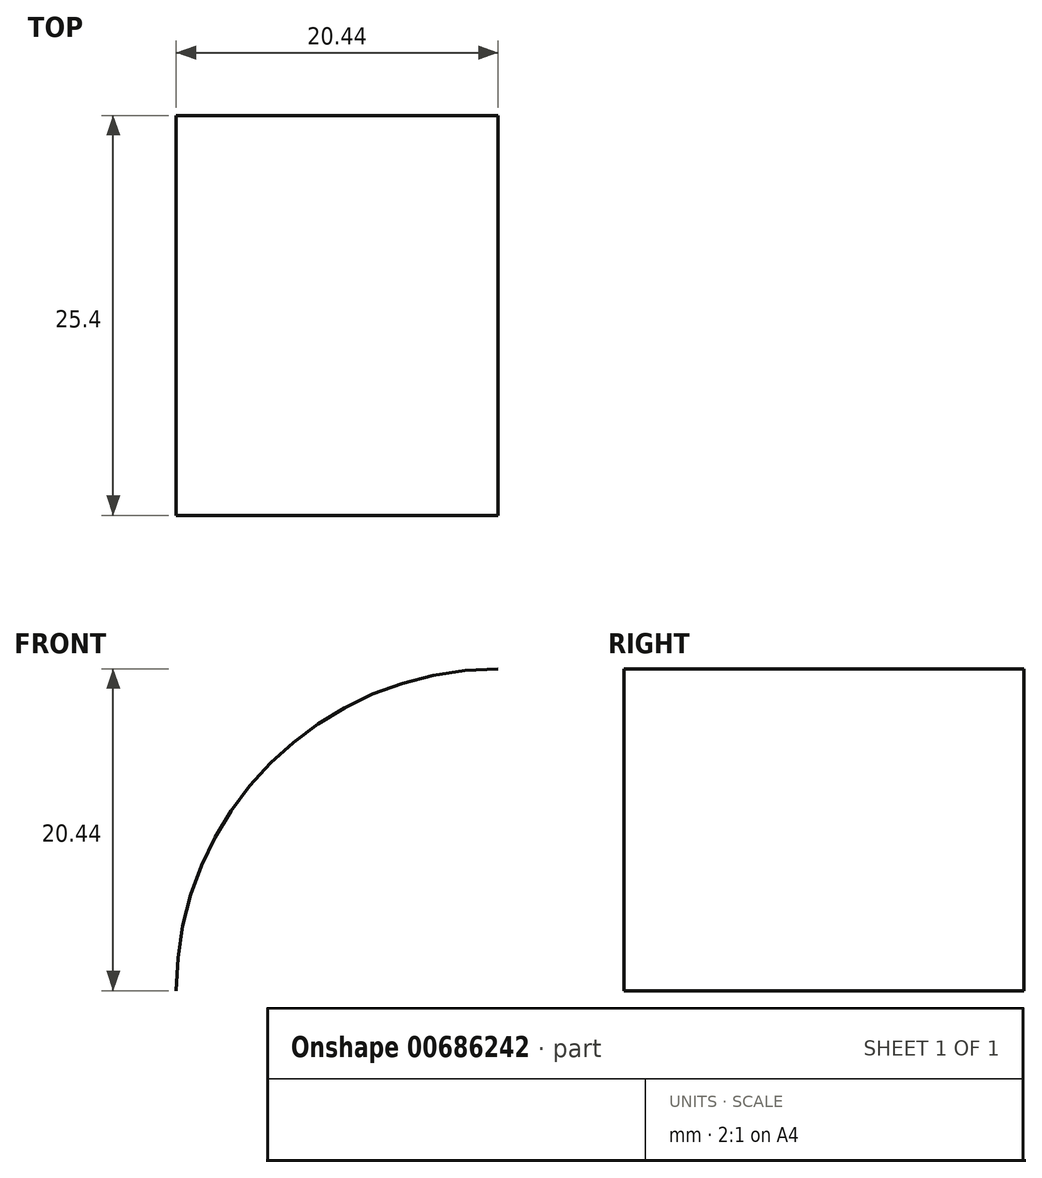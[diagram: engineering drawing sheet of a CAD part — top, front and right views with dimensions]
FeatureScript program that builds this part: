
annotation { "Feature Type Name" : "Feature", "Feature Type Description" : "" }
export const myFeature = defineFeature(function(context is Context, id is Id, definition is map)
    precondition{}
    {
        {
            var Q0;
            Q0=qCreatedBy(makeId("Front.planeOp"),FACE);
            var sketch = newSketch(context, id + "F0", { "sketchPlane" : qUnion([Q0])});
            skLineSegment(sketch, "E0.bottom", {"start": v(-53.76, 12.38) * mm, "end": v(22.44, 12.38) * mm});
            skLineSegment(sketch, "E0.top", {"start": v(-53.76, -12.77) * mm, "end": v(22.44, -12.77) * mm});
            skLineSegment(sketch, "E0.left", {"start": v(-53.76, 12.38) * mm, "end": v(-53.76, -12.77) * mm});
            skLineSegment(sketch, "E0.right", {"start": v(22.44, 12.38) * mm, "end": v(22.44, -12.77) * mm});
            skLineSegment(sketch, "E1.bottom", {"start": v(47.84, 45.71) * mm, "end": v(73.57, 45.71) * mm});
            skLineSegment(sketch, "E1.top", {"start": v(47.84, 25.57) * mm, "end": v(73.57, 25.57) * mm});
            skLineSegment(sketch, "E1.left", {"start": v(47.84, 45.71) * mm, "end": v(47.84, 25.57) * mm});
            skLineSegment(sketch, "E1.right", {"start": v(73.57, 45.71) * mm, "end": v(73.57, 25.57) * mm});
            skLineSegment(sketch, "E2", {"start": v(22.44, 12.38) * mm, "end": v(22.44, 20) * mm});
            skArc(sketch, "E3", {"start": v(22.44, 20) * mm, "mid": v(26.9, 30.77) * mm, "end": v(37.68, 35.24) * mm});
            skLineSegment(sketch, "E4", {"start": v(37.68, 35.24) * mm, "end": v(60.87, 35.24) * mm});
            skLineSegment(sketch, "E5.0", {"start": v(37.68, 40.44) * mm, "end": v(60.87, 40.44) * mm});
            skArc(sketch, "E5.1", {"start": v(17.24, 20) * mm, "mid": v(23.23, 34.45) * mm, "end": v(37.68, 40.44) * mm});
            skLineSegment(sketch, "E5.2", {"start": v(17.24, 12.2) * mm, "end": v(17.24, 20) * mm});
            skSolve(sketch);
        }
        {
            var Q0;
            Q0=sQuery(id+"F0.wireOp",EDGE,"E5.1");
            extrude(context, id + "F1", {"bodyType" : ToolBodyType.SURFACE, "surfaceEntities" : qUnion([Q0]), "depth" : 25.4 * mm, "offsetDistance" : 25.4 * mm});
        }
    });
